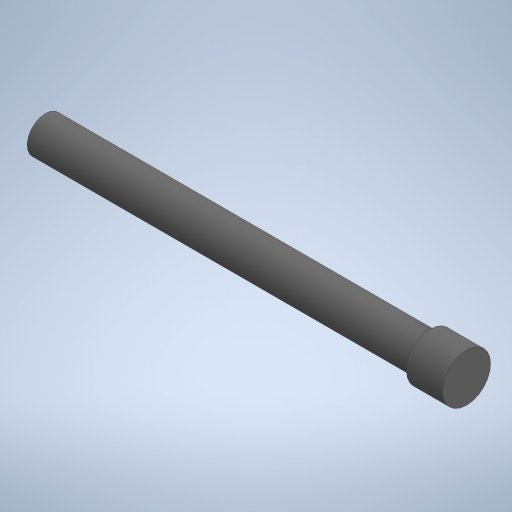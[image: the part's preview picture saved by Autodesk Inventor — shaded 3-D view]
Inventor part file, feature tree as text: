
AUTODESK INVENTOR PART (.ipt)
format: ipt  version: 2024 (Build 280153000, 153)  size: 237,568 bytes
history: native  units: in
note: dims shown in document units (in); Inventor stores cm internally (conversion verified against a paired STEP export)
features: extrude x2, sketch x2
ambient origin geometry x8: Origin, YZ Plane, XZ Plane, XY Plane, X Axis, Y Axis, Z Axis, Center Point
bodies: Solid1 (feature_tree)
feature tree (4):
  extrude  "Extrusion1"  Depth=2.0in TaperAngle=0.0deg
  extrude  "Extrusion2"  Depth=0.1875in TaperAngle=0.0deg
  sketch  "Sketch1"  dims[d0=0.19in d1=2.0in d2=0.0in]
  sketch  "Sketch2"  dims[d3=0.25in d4=0.1875in d5=0.0in]
